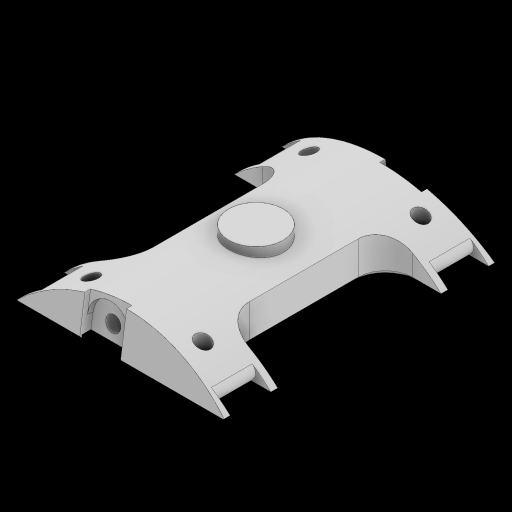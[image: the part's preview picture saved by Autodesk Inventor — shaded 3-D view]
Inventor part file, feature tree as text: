
AUTODESK INVENTOR PART (.ipt)
format: ipt  version: 2023 (Build 270158000, 158)  size: 411,136 bytes
history: native  units: mm
features: extrude x15, sketch x6, fillet x2, chamfer x1, plane x1, hole x1
ambient origin geometry x8: Origin, YZ Plane, XZ Plane, XY Plane, X Axis, Y Axis, Z Axis, Center Point
bodies: Solid1 (feature_tree)
feature tree (26):
  sketch  "Sketch1"  dims[d0=5.5mm d1=15.0mm d2=20.0mm]
  extrude  "Extrusion1"  Depth=20.0mm
  extrude  "Extrusion2"  Depth=17.0mm TaperAngle=0.0deg
  fillet  "Fillet2"  Radius=2.0mm
  chamfer  "Chamfer1"  Distance=200.0mm
  plane  "Work Plane1"
  extrude  "Extrusion3"  Depth=10.0mm
  extrude  "Extrusion4"  TaperAngle=90.0deg  [1 undecoded]
  extrude  "Extrusion5"  TaperAngle=90.0deg  [1 undecoded]
  extrude  "Extrusion6"  Depth=10.93871mm
  sketch  "Sketch4"  dims[d18=100.0mm d20=90.0deg]
  extrude  "Extrusion10"  Depth=2.0mm
  extrude  "Extrusion11"  Depth=200.0mm TaperAngle=0.0deg
  extrude  "Extrusion12"  Depth=2.0mm TaperAngle=0.0deg
  sketch  "Sketch5"  dims[d21=260.34779mm d22=90.0deg]
  extrude  "Extrusion13"  Depth=3.0mm TaperAngle=0.0deg
  extrude  "Extrusion14"  Depth=15.0mm TaperAngle=0.0deg
  extrude  "Extrusion15"  Depth=15.0mm
  hole  "Hole1"  [1 undecoded]
  fillet  "Fillet4"  Radius=2.0mm
  extrude  "Extrusion16"  TaperAngle=90.0deg  [1 undecoded]
  extrude  "Extrusion17"  Depth=15.0mm
  extrude  "Extrusion18"  Depth=15.0mm
  sketch  "Sketch2"  dims[d4=35.0mm d5=17.0mm d6=0.0mm d7=2.0mm d10=200.0mm d11=0.0mm]
  sketch  "Sketch3"  dims[d13=10.0mm d14=2.0mm d15=4.0mm d16=13.962634mm]
  sketch  "Sketch6"  dims[d23=47.979859mm d24=10.93871mm d25=2.0mm d26=200.0mm d27=0.0mm d28=2.0mm d29=0.0mm d30=3.0mm d31=0.0mm d32=15.0mm d33=0.0mm d35=15.0mm d36=90.0deg d37=2.0mm d38=90.0deg d39=15.0mm d40=15.0mm d41=5.5mm d42=20.0mm d49=4.0mm d50=0.0mm d51=2.0mm d52=2.0mm d53=0.0mm d54=20.0mm d55=0.0mm d56=15.0mm d57=90.0deg d58=2.0mm d59=90.0deg d60=15.0mm d61=15.0mm d62=5.5mm d63=20.0mm d64=2.0mm d65=2.0mm d66=0.0mm d67=4.0mm d68=0.0mm d69=20.0mm d70=0.0mm d72=8.0mm d73=6.0mm d74=20.0mm d75=2.0mm d76=90.0deg d77=20.0mm d78=0.0mm d79=3.0mm d82=7.5mm d83=244.423mm d84=41.005864mm d85=18.0mm d86=264.926mm d87=0.0mm d88=15.0mm d89=2.0mm d90=0.0mm d91=1.0mm d92=0.0mm d93=20.0mm d94=0.0mm d8=0.872665mm d17=0.0mm d19=0.0mm d71=0.0mm d80=0.0mm d81=0.0mm]
note: 4 required parameter values undecoded (feature->parameter linkage not recoverable at this tier; creation-order binding heuristic only, values carry confidence <= 0.55)
